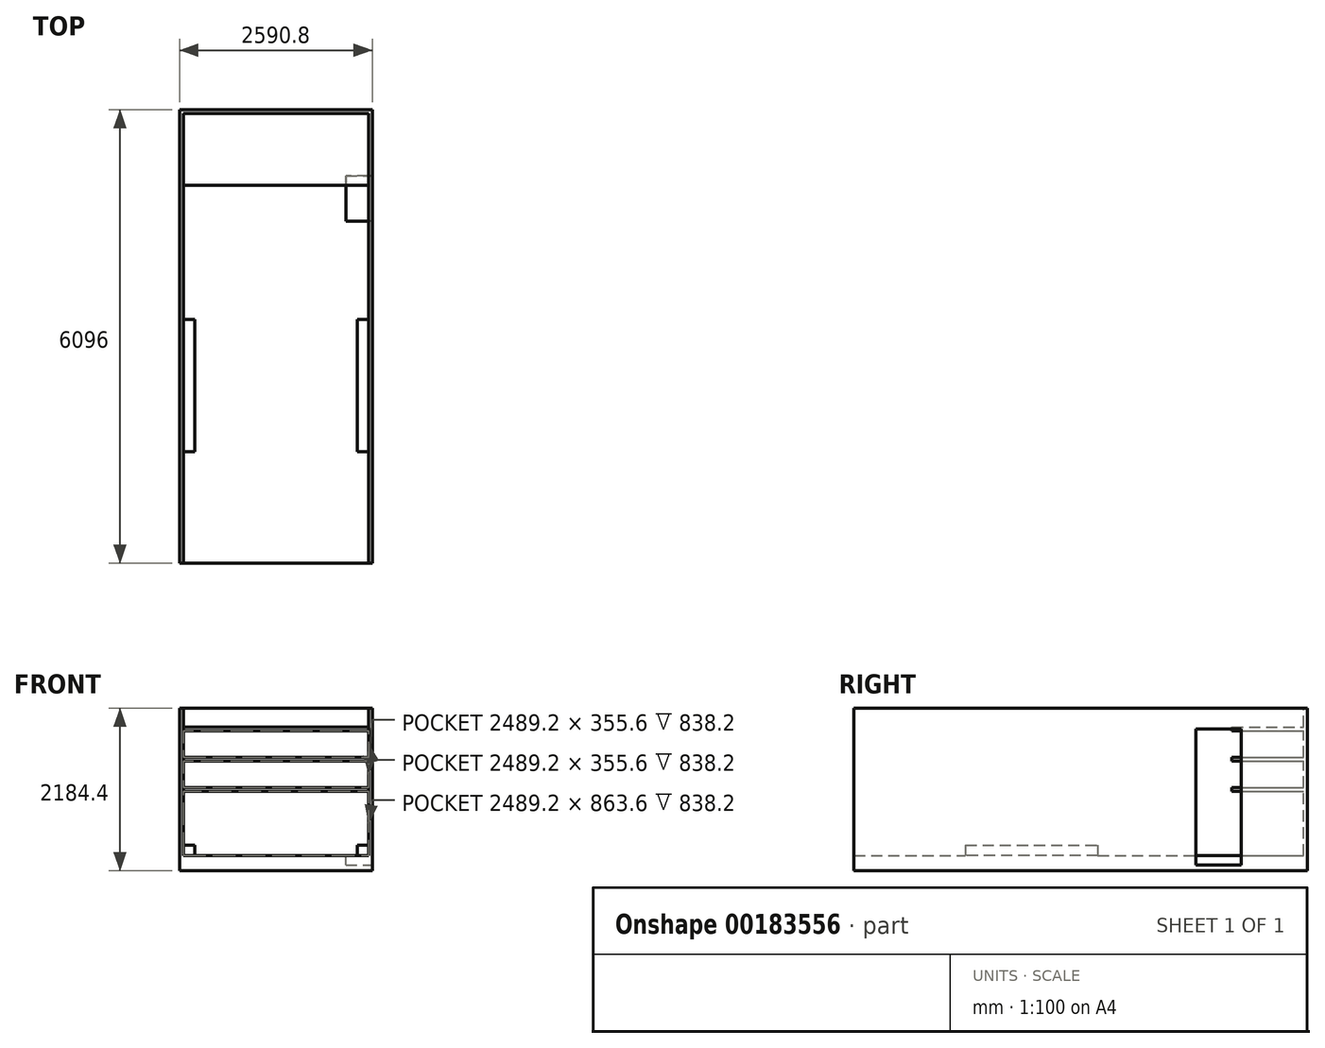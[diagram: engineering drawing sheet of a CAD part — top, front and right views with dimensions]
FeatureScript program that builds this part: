
annotation { "Feature Type Name" : "Feature", "Feature Type Description" : "" }
export const myFeature = defineFeature(function(context is Context, id is Id, definition is map)
    precondition{}
    {
        {
            var Q0;
            Q0=qCreatedBy(makeId("Front.planeOp"),FACE);
            var sketch = newSketch(context, id + "F0", { "sketchPlane" : qUnion([Q0])});
            skLineSegment(sketch, "E0.bottom", {"start": v(1295.4, 990.6) * mm, "end": v(-1295.4, 990.6) * mm});
            skLineSegment(sketch, "E0.top", {"start": v(1295.4, -990.6) * mm, "end": v(-1295.4, -990.6) * mm});
            skLineSegment(sketch, "E0.left", {"start": v(1295.4, 990.6) * mm, "end": v(1295.4, -990.6) * mm});
            skLineSegment(sketch, "E0.right", {"start": v(-1295.4, 990.6) * mm, "end": v(-1295.4, -990.6) * mm});
            skPoint(sketch, "E0.middle", {"position": v(0, 0) * mm});
            skSolve(sketch);
        }
        {
            var Q0;
            Q0=makeQuery(id+"F0.imprint","IMPRINT",FACE,{"disambiguationData":[TD([[makeQuery(id+"F0.imprint","IMPRINT",EDGE,{"derivedFrom":sQuery(id+"F0.wireOp",EDGE,"E0.bottom")}),1.0]])]});
            extrude(context, id + "F1", {"entities" : qUnion([Q0]), "oppositeDirection" : true, "depth" : 6096 * mm});
        }
        {
            var Q0;
            Q0=makeQuery(id+"F1.opExtrude","CAP_FACE",FACE,{"disambiguationData":[OSD([sQuery(id+"F0.wireOp",EDGE,"E0.bottom"),sQuery(id+"F0.wireOp",EDGE,"E0.top"),sQuery(id+"F0.wireOp",EDGE,"E0.left"),sQuery(id+"F0.wireOp",EDGE,"E0.right")])],"isStart":true});
            var sketch = newSketch(context, id + "F2", { "sketchPlane" : qUnion([Q0])});
            skLineSegment(sketch, "E1.bottom", {"start": v(-1244.6, -1244.6) * mm, "end": v(1244.6, -1244.6) * mm});
            skLineSegment(sketch, "E1.top", {"start": v(-1244.6, 1244.6) * mm, "end": v(1244.6, 1244.6) * mm});
            skLineSegment(sketch, "E1.left", {"start": v(-1244.6, -1244.6) * mm, "end": v(-1244.6, 1244.6) * mm});
            skLineSegment(sketch, "E1.right", {"start": v(1244.6, -1244.6) * mm, "end": v(1244.6, 1244.6) * mm});
            skPoint(sketch, "E1.middle", {"position": v(0, 0) * mm});
            skSolve(sketch);
        }
        {
            var Q0;
            Q0 = qSketchRegion(id + "F2", true);
            extrude(context, id + "F3", {"entities" : qUnion([Q0]), "operationType" : NewBodyOperationType.REMOVE, "oppositeDirection" : true, "depth" : 6045.2 * mm});
        }
        {
            var Q0;
            Q0=makeQuery(id+"F1.opExtrude","SWEPT_FACE",FACE,{"disambiguationData":[OSD([sQuery(id+"F0.wireOp",EDGE,"E0.bottom")])]});
            var sketch = newSketch(context, id + "F4", { "sketchPlane" : qUnion([Q0])});
            skLineSegment(sketch, "E2.bottom", {"start": v(-1244.6, 6045.2) * mm, "end": v(1244.6, 6045.2) * mm});
            skLineSegment(sketch, "E2.top", {"start": v(-1244.6, 0) * mm, "end": v(1244.6, 0) * mm});
            skLineSegment(sketch, "E2.left", {"start": v(-1244.6, 6045.2) * mm, "end": v(-1244.6, 0) * mm});
            skLineSegment(sketch, "E2.right", {"start": v(1244.6, 6045.2) * mm, "end": v(1244.6, 0) * mm});
            skSolve(sketch);
        }
        {
            var Q0;
            Q0 = qSketchRegion(id + "F4", true);
            extrude(context, id + "F5", {"entities" : qUnion([Q0]), "operationType" : NewBodyOperationType.REMOVE, "oppositeDirection" : true, "depth" : 76.2 * mm});
        }
        {
            var Q0;
            Q0=makeQuery(id+"F1.opExtrude","SWEPT_FACE",FACE,{"disambiguationData":[OSD([sQuery(id+"F0.wireOp",EDGE,"E0.top")])]});
            var sketch = newSketch(context, id + "F6", { "sketchPlane" : qUnion([Q0])});
            skLineSegment(sketch, "E3.bottom", {"start": v(-1295.4, 0) * mm, "end": v(1295.4, 0) * mm});
            skLineSegment(sketch, "E3.top", {"start": v(-1295.4, -6096) * mm, "end": v(1295.4, -6096) * mm});
            skLineSegment(sketch, "E3.left", {"start": v(-1295.4, 0) * mm, "end": v(-1295.4, -6096) * mm});
            skLineSegment(sketch, "E3.right", {"start": v(1295.4, 0) * mm, "end": v(1295.4, -6096) * mm});
            skSolve(sketch);
        }
        {
            var Q0;
            Q0 = qSketchRegion(id + "F6", true);
            extrude(context, id + "F7", {"entities" : qUnion([Q0]), "operationType" : NewBodyOperationType.ADD, "depth" : 127 * mm});
        }
        {
            var Q0;
            Q0=makeQuery(id+"F7.opExtrude","CAP_FACE",FACE,{"disambiguationData":[OSD([sQuery(id+"F6.wireOp",EDGE,"E3.bottom"),sQuery(id+"F6.wireOp",EDGE,"E3.top"),sQuery(id+"F6.wireOp",EDGE,"E3.left"),sQuery(id+"F6.wireOp",EDGE,"E3.right")])],"isStart":true});
            var sketch = newSketch(context, id + "F8", { "sketchPlane" : qUnion([Q0])});
            skLineSegment(sketch, "E4.bottom", {"start": v(1244.6, 5207) * mm, "end": v(939.8, 5207) * mm});
            skLineSegment(sketch, "E4.top", {"start": v(1244.6, 4597.4) * mm, "end": v(939.8, 4597.4) * mm});
            skLineSegment(sketch, "E4.left", {"start": v(1244.6, 5207) * mm, "end": v(1244.6, 4597.4) * mm});
            skLineSegment(sketch, "E4.right", {"start": v(939.8, 5207) * mm, "end": v(939.8, 4597.4) * mm});
            skSolve(sketch);
        }
        {
            var Q0;
            Q0 = qSketchRegion(id + "F8", true);
            extrude(context, id + "F9", {"entities" : qUnion([Q0]), "operationType" : NewBodyOperationType.REMOVE, "oppositeDirection" : true, "depth" : 139.7 * mm});
        }
        {
            var Q0;
            Q0=makeQuery(id+"F7.opExtrude","CAP_FACE",FACE,{"disambiguationData":[OSD([sQuery(id+"F6.wireOp",EDGE,"E3.bottom"),sQuery(id+"F6.wireOp",EDGE,"E3.top"),sQuery(id+"F6.wireOp",EDGE,"E3.left"),sQuery(id+"F6.wireOp",EDGE,"E3.right")])],"isStart":false});
            var sketch = newSketch(context, id + "F10", { "sketchPlane" : qUnion([Q0])});
            skLineSegment(sketch, "E5.bottom", {"start": v(-1295.4, 0) * mm, "end": v(1295.4, 0) * mm});
            skLineSegment(sketch, "E5.top", {"start": v(-1295.4, -6096) * mm, "end": v(1295.4, -6096) * mm});
            skLineSegment(sketch, "E5.left", {"start": v(-1295.4, 0) * mm, "end": v(-1295.4, -6096) * mm});
            skLineSegment(sketch, "E5.right", {"start": v(1295.4, 0) * mm, "end": v(1295.4, -6096) * mm});
            skSolve(sketch);
        }
        {
            var Q0;
            Q0 = qSketchRegion(id + "F10", true);
            extrude(context, id + "F11", {"entities" : qUnion([Q0]), "operationType" : NewBodyOperationType.ADD, "depth" : 76.2 * mm});
        }
        {
            var Q0;
            Q0=makeQuery(id+"F7.opExtrude","CAP_FACE",FACE,{"disambiguationData":[OSD([sQuery(id+"F6.wireOp",EDGE,"E3.bottom"),sQuery(id+"F6.wireOp",EDGE,"E3.top"),sQuery(id+"F6.wireOp",EDGE,"E3.left"),sQuery(id+"F6.wireOp",EDGE,"E3.right")])],"isStart":true});
            var sketch = newSketch(context, id + "F12", { "sketchPlane" : qUnion([Q0])});
            skLineSegment(sketch, "E6", {"start": v(0, 6045.2) * mm, "end": v(0, 0) * mm, "construction": true});
            skLineSegment(sketch, "E7.bottom", {"start": v(1244.6, 3276.6) * mm, "end": v(1092.2, 3276.6) * mm});
            skLineSegment(sketch, "E7.top", {"start": v(1244.6, 1498.6) * mm, "end": v(1092.2, 1498.6) * mm});
            skLineSegment(sketch, "E7.left", {"start": v(1244.6, 3276.6) * mm, "end": v(1244.6, 1498.6) * mm});
            skLineSegment(sketch, "E7.right", {"start": v(1092.2, 3276.6) * mm, "end": v(1092.2, 1498.6) * mm});
            skLineSegment(sketch, "E8.MirrorCS", {"start": v(-1244.6, 3276.6) * mm, "end": v(-1092.2, 3276.6) * mm});
            skLineSegment(sketch, "E9.MirrorCS", {"start": v(-1244.6, 3276.6) * mm, "end": v(-1244.6, 1498.6) * mm});
            skLineSegment(sketch, "E10.MirrorCS", {"start": v(-1092.2, 3276.6) * mm, "end": v(-1092.2, 1498.6) * mm});
            skLineSegment(sketch, "E11.MirrorCS", {"start": v(-1244.6, 1498.6) * mm, "end": v(-1092.2, 1498.6) * mm});
            skSolve(sketch);
        }
        {
            var Q0;
            Q0 = qSketchRegion(id + "F12", true);
            extrude(context, id + "F13", {"entities" : qUnion([Q0]), "operationType" : NewBodyOperationType.ADD, "depth" : 139.7 * mm});
        }
        {
            var Q0;
            Q0=makeQuery(id+"F3.boolean.opBoolean","COPY",FACE,{"derivedFrom":makeQuery(id+"F3.opExtrude","CAP_FACE",FACE,{"disambiguationData":[OSD([sQuery(id+"F2.wireOp",EDGE,"E1.bottom"),sQuery(id+"F2.wireOp",EDGE,"E1.top"),sQuery(id+"F2.wireOp",EDGE,"E1.left"),sQuery(id+"F2.wireOp",EDGE,"E1.right")])],"isStart":false})});
            var sketch = newSketch(context, id + "F14", { "sketchPlane" : qUnion([Q0])});
            skLineSegment(sketch, "E12.bottom", {"start": v(-1244.6, 736.6) * mm, "end": v(1244.6, 736.6) * mm});
            skLineSegment(sketch, "E12.top", {"start": v(-1244.6, 685.8) * mm, "end": v(1244.6, 685.8) * mm});
            skLineSegment(sketch, "E12.left", {"start": v(-1244.6, 736.6) * mm, "end": v(-1244.6, 685.8) * mm});
            skLineSegment(sketch, "E12.right", {"start": v(1244.6, 736.6) * mm, "end": v(1244.6, 685.8) * mm});
            skLineSegment(sketch, "E13.0.1.0", {"start": v(-1244.6, 330.2) * mm, "end": v(1244.6, 330.2) * mm});
            skLineSegment(sketch, "E13.0.1.1", {"start": v(-1244.6, 279.4) * mm, "end": v(1244.6, 279.4) * mm});
            skLineSegment(sketch, "E13.0.1.2", {"start": v(-1244.6, 330.2) * mm, "end": v(-1244.6, 279.4) * mm});
            skLineSegment(sketch, "E13.0.1.3", {"start": v(1244.6, 330.2) * mm, "end": v(1244.6, 279.4) * mm});
            skLineSegment(sketch, "E13.0.2.0", {"start": v(-1244.6, -76.2) * mm, "end": v(1244.6, -76.2) * mm});
            skLineSegment(sketch, "E13.0.2.1", {"start": v(-1244.6, -127) * mm, "end": v(1244.6, -127) * mm});
            skLineSegment(sketch, "E13.0.2.2", {"start": v(-1244.6, -76.2) * mm, "end": v(-1244.6, -127) * mm});
            skLineSegment(sketch, "E13.0.2.3", {"start": v(1244.6, -76.2) * mm, "end": v(1244.6, -127) * mm});
            skLineSegment(sketch, "E13.direction1", {"start": v(-1244.6, 736.6) * mm, "end": v(-1219.2, 736.6) * mm, "construction": true});
            skLineSegment(sketch, "E13.direction2", {"start": v(-1244.6, 736.6) * mm, "end": v(-1244.6, 330.2) * mm, "construction": true});
            skSolve(sketch);
        }
        {
            var Q0;
            Q0 = qSketchRegion(id + "F14", true);
            extrude(context, id + "F15", {"entities" : qUnion([Q0]), "operationType" : NewBodyOperationType.ADD, "depth" : 965.2 * mm});
        }
        {
            var Q0;
            Q0=makeQuery(id+"F9.boolean.opBoolean","MERGE",FACE,{"derivedFrom":[makeQuery(id+"F3.boolean.opBoolean","COPY",FACE,{"derivedFrom":makeQuery(id+"F3.opExtrude","SWEPT_FACE",FACE,{"disambiguationData":[OSD([sQuery(id+"F2.wireOp",EDGE,"E1.right")])]})}),makeQuery(id+"F9.opExtrude","SWEPT_FACE",FACE,{"disambiguationData":[OSD([sQuery(id+"F8.wireOp",EDGE,"E4.left")])]})]});
            var sketch = newSketch(context, id + "F16", { "sketchPlane" : qUnion([Q0])});
            skLineSegment(sketch, "E14", {"start": v(-5207, -1117.6) * mm, "end": v(-5207, 990.6) * mm, "construction": true});
            skLineSegment(sketch, "E15", {"start": v(-4597.4, -1117.6) * mm, "end": v(-4597.4, 990.6) * mm, "construction": true});
            skLineSegment(sketch, "E16.bottom", {"start": v(-5207, -1117.6) * mm, "end": v(-4597.4, -1117.6) * mm});
            skLineSegment(sketch, "E16.top", {"start": v(-5207, 711.2) * mm, "end": v(-4597.4, 711.2) * mm});
            skLineSegment(sketch, "E16.left", {"start": v(-5207, -1117.6) * mm, "end": v(-5207, 711.2) * mm});
            skLineSegment(sketch, "E16.right", {"start": v(-4597.4, -1117.6) * mm, "end": v(-4597.4, 711.2) * mm});
            skSolve(sketch);
        }
        {
            var Q0;
            Q0 = qSketchRegion(id + "F16", true);
            extrude(context, id + "F17", {"entities" : qUnion([Q0]), "operationType" : NewBodyOperationType.REMOVE, "endBound" : BoundingType.THROUGH_ALL, "oppositeDirection" : true, "depth" : 25.4 * mm});
        }
    });
